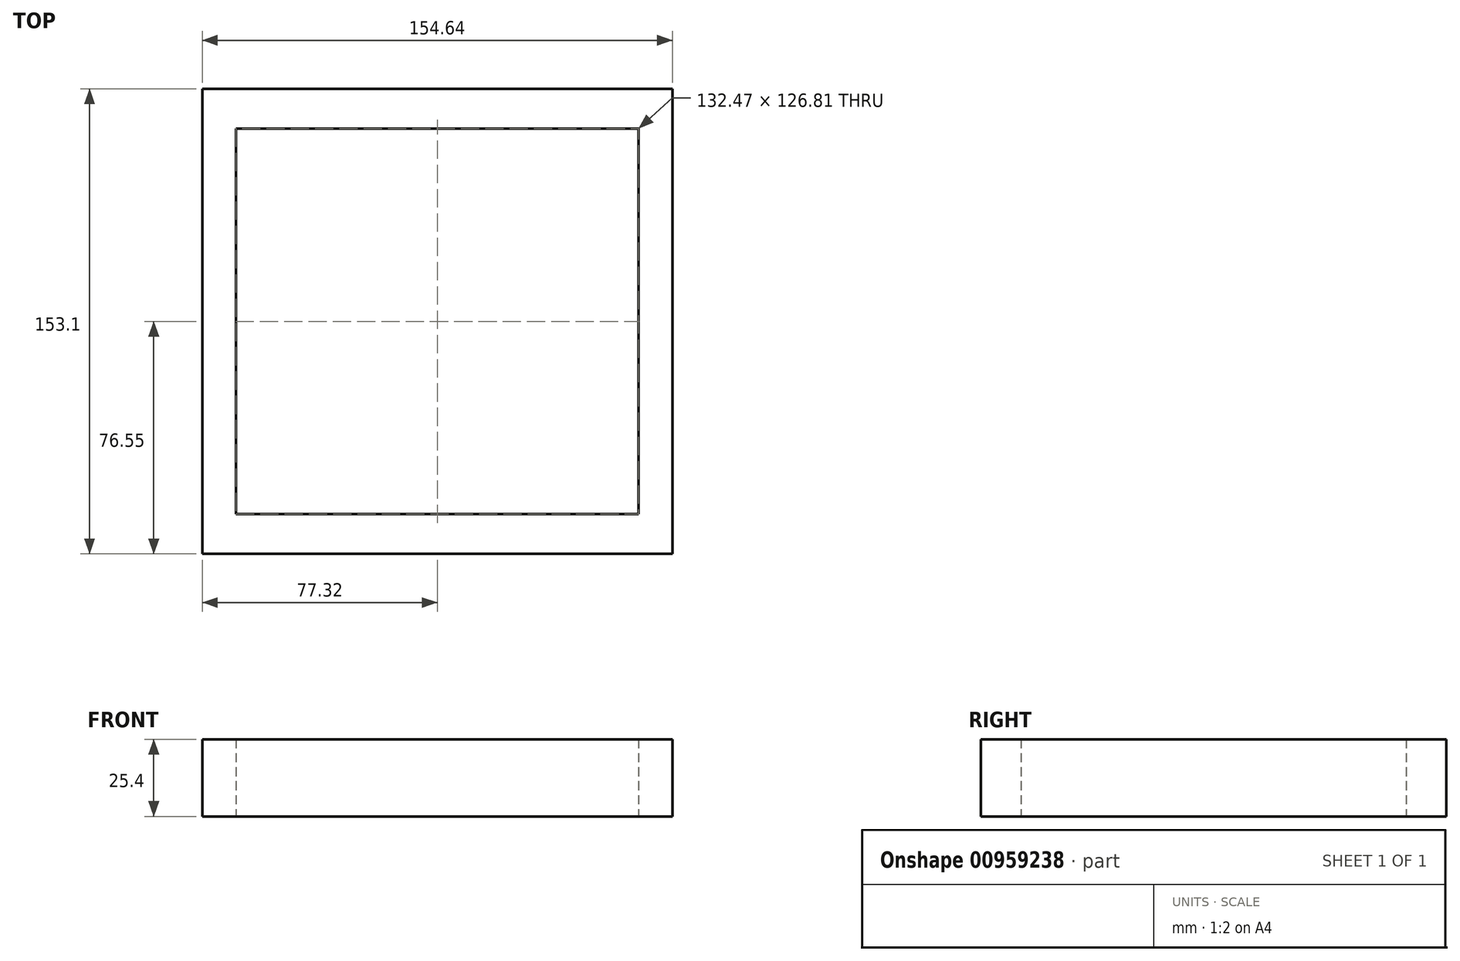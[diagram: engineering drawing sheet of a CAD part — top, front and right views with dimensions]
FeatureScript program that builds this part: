
annotation { "Feature Type Name" : "Feature", "Feature Type Description" : "" }
export const myFeature = defineFeature(function(context is Context, id is Id, definition is map)
    precondition{}
    {
        {
            var Q0;
            Q0=qCreatedBy(makeId("Top.planeOp"),FACE);
            var sketch = newSketch(context, id + "F0", { "sketchPlane" : qUnion([Q0])});
            skLineSegment(sketch, "E0.bottom", {"start": v(77.32, 76.55) * mm, "end": v(-77.32, 76.55) * mm});
            skLineSegment(sketch, "E0.top", {"start": v(77.32, -76.55) * mm, "end": v(-77.32, -76.55) * mm});
            skLineSegment(sketch, "E0.left", {"start": v(77.32, 76.55) * mm, "end": v(77.32, -76.55) * mm});
            skLineSegment(sketch, "E0.right", {"start": v(-77.32, 76.55) * mm, "end": v(-77.32, -76.55) * mm});
            skPoint(sketch, "E0.middle", {"position": v(0, 0) * mm});
            skSolve(sketch);
        }
        {
            var Q0;
            Q0 = qSketchRegion(id + "F0", true);
            var sketch = newSketch(context, id + "F1", { "sketchPlane" : qUnion([Q0])});
            skLineSegment(sketch, "E1.bottom", {"start": v(66.23, 63.4) * mm, "end": v(-66.23, 63.4) * mm});
            skLineSegment(sketch, "E1.top", {"start": v(66.23, -63.4) * mm, "end": v(-66.23, -63.4) * mm});
            skLineSegment(sketch, "E1.left", {"start": v(66.23, 63.4) * mm, "end": v(66.23, -63.4) * mm});
            skLineSegment(sketch, "E1.right", {"start": v(-66.23, 63.4) * mm, "end": v(-66.23, -63.4) * mm});
            skPoint(sketch, "E1.middle", {"position": v(0, 0) * mm});
            skSolve(sketch);
        }
        {
            var Q0;
            Q0=makeQuery(id+"F1.imprint","IMPRINT",FACE,{"disambiguationData":[TD([[makeQuery(id+"F1.imprint","IMPRINT",EDGE,{"derivedFrom":sQuery(id+"F1.wireOp",EDGE,"E1.bottom")}),-1.0]])]});
            extrude(context, id + "F2", {"entities" : qUnion([Q0]), "depth" : 25.4 * mm, "offsetDistance" : 25.4 * mm});
        }
    });
